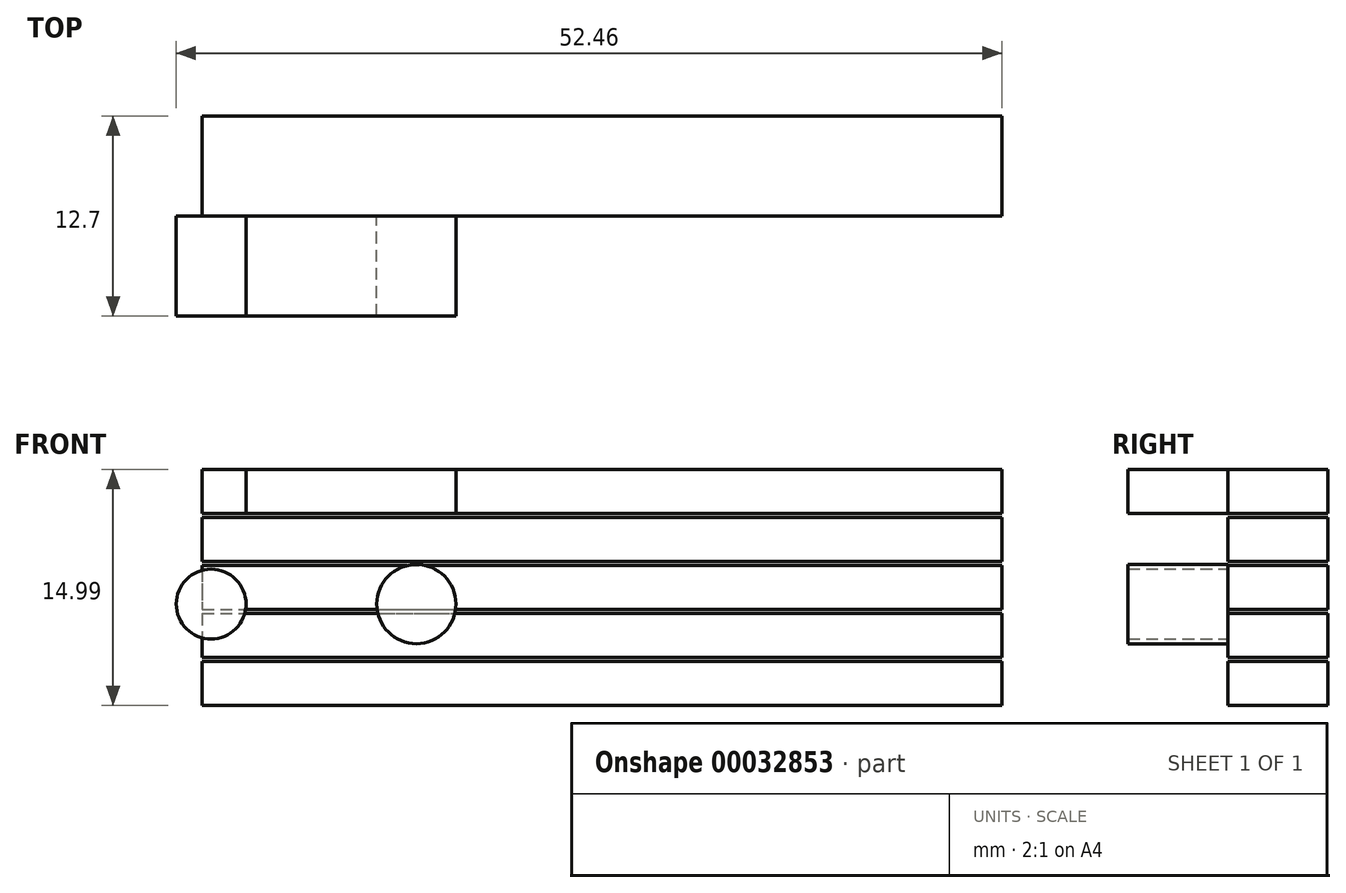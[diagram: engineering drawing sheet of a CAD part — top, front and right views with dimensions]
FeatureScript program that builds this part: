
annotation { "Feature Type Name" : "Feature", "Feature Type Description" : "" }
export const myFeature = defineFeature(function(context is Context, id is Id, definition is map)
    precondition{}
    {
        {
            var Q0;
            Q0=qCreatedBy(makeId("Front.planeOp"),FACE);
            var sketch = newSketch(context, id + "F0", { "sketchPlane" : qUnion([Q0])});
            skLineSegment(sketch, "E0.bottom", {"start": v(-26.57, 14.99) * mm, "end": v(24.23, 14.99) * mm});
            skLineSegment(sketch, "E0.top", {"start": v(-26.57, 12.2) * mm, "end": v(24.23, 12.2) * mm});
            skLineSegment(sketch, "E0.left", {"start": v(-26.57, 14.99) * mm, "end": v(-26.57, 12.2) * mm});
            skLineSegment(sketch, "E0.right", {"start": v(24.23, 14.99) * mm, "end": v(24.23, 12.2) * mm});
            skLineSegment(sketch, "E1.bottom", {"start": v(-26.57, 11.94) * mm, "end": v(24.23, 11.94) * mm});
            skLineSegment(sketch, "E1.top", {"start": v(-26.57, 9.14) * mm, "end": v(24.23, 9.14) * mm});
            skLineSegment(sketch, "E1.left", {"start": v(-26.57, 11.94) * mm, "end": v(-26.57, 9.14) * mm});
            skLineSegment(sketch, "E1.right", {"start": v(24.23, 11.94) * mm, "end": v(24.23, 9.14) * mm});
            skLineSegment(sketch, "E2.bottom", {"start": v(-26.57, 8.89) * mm, "end": v(24.23, 8.89) * mm});
            skLineSegment(sketch, "E2.top", {"start": v(-26.57, 6.1) * mm, "end": v(24.23, 6.1) * mm});
            skLineSegment(sketch, "E2.left", {"start": v(-26.57, 8.89) * mm, "end": v(-26.57, 6.1) * mm});
            skLineSegment(sketch, "E2.right", {"start": v(24.23, 8.89) * mm, "end": v(24.23, 6.1) * mm});
            skLineSegment(sketch, "E3.bottom", {"start": v(-26.57, 5.84) * mm, "end": v(24.23, 5.84) * mm});
            skLineSegment(sketch, "E3.top", {"start": v(-26.57, 3.05) * mm, "end": v(24.23, 3.05) * mm});
            skLineSegment(sketch, "E3.left", {"start": v(-26.57, 5.84) * mm, "end": v(-26.57, 3.05) * mm});
            skLineSegment(sketch, "E3.right", {"start": v(24.23, 5.84) * mm, "end": v(24.23, 3.05) * mm});
            skLineSegment(sketch, "E4.bottom", {"start": v(-26.57, 2.8) * mm, "end": v(24.23, 2.8) * mm});
            skLineSegment(sketch, "E4.top", {"start": v(-26.57, 0) * mm, "end": v(24.23, 0) * mm});
            skLineSegment(sketch, "E4.left", {"start": v(-26.57, 2.8) * mm, "end": v(-26.57, 0) * mm});
            skLineSegment(sketch, "E4.right", {"start": v(24.23, 2.8) * mm, "end": v(24.23, 0) * mm});
            skSolve(sketch);
        }
        {
            var Q0;
            Q0 = qSketchRegion(id + "F0", true);
            extrude(context, id + "F1", {"entities" : qUnion([Q0]), "depth" : 6.35 * mm});
        }
        {
            var Q0;
            Q0=makeQuery(id+"F1.opExtrude","CAP_FACE",FACE,{"disambiguationData":[OSD([sQuery(id+"F0.wireOp",EDGE,"E0.bottom"),sQuery(id+"F0.wireOp",EDGE,"E0.top"),sQuery(id+"F0.wireOp",EDGE,"E0.left"),sQuery(id+"F0.wireOp",EDGE,"E0.right")])],"isStart":false});
            var sketch = newSketch(context, id + "F2", { "sketchPlane" : qUnion([Q0])});
            skLineSegment(sketch, "E5.bottom", {"start": v(-23.8, 14.99) * mm, "end": v(-10.46, 14.99) * mm});
            skLineSegment(sketch, "E5.top", {"start": v(-23.8, 12.2) * mm, "end": v(-10.46, 12.2) * mm});
            skLineSegment(sketch, "E5.left", {"start": v(-23.8, 14.99) * mm, "end": v(-23.8, 12.2) * mm});
            skLineSegment(sketch, "E5.right", {"start": v(-10.46, 14.99) * mm, "end": v(-10.46, 12.2) * mm});
            skLineSegment(sketch, "E6.bottom", {"start": v(-23.8, 14.99) * mm, "end": v(-23.8, 14.99) * mm});
            skLineSegment(sketch, "E6.top", {"start": v(-23.8, 6.44) * mm, "end": v(-23.8, 6.44) * mm});
            skLineSegment(sketch, "E6.left", {"start": v(-23.8, 14.99) * mm, "end": v(-23.8, 6.44) * mm});
            skLineSegment(sketch, "E6.right", {"start": v(-23.8, 14.99) * mm, "end": v(-23.8, 6.44) * mm});
            skLineSegment(sketch, "E7.bottom", {"start": v(-10.46, 14.99) * mm, "end": v(-10.46, 14.99) * mm});
            skLineSegment(sketch, "E7.top", {"start": v(-10.46, 6.44) * mm, "end": v(-10.46, 6.44) * mm});
            skLineSegment(sketch, "E7.left", {"start": v(-10.46, 14.99) * mm, "end": v(-10.46, 6.44) * mm});
            skLineSegment(sketch, "E7.right", {"start": v(-10.46, 14.99) * mm, "end": v(-10.46, 6.44) * mm});
            skCircle(sketch, "E8", {"center": v(-26, 6.44) * mm, "radius": 2.22 * mm});
            skCircle(sketch, "E9", {"center": v(-12.97, 6.44) * mm, "radius": 2.52 * mm});
            skSolve(sketch);
        }
        {
            var Q0;
            Q0 = qSketchRegion(id + "F2", true);
            extrude(context, id + "F3", {"entities" : qUnion([Q0]), "depth" : 6.35 * mm});
        }
    });
